# Revit family: Hager-VEGA-Surface_mounted-IP40-With_Cover-With_DIN-Hosted-ES-es
name_source: partatom
category: Electrical Equipment
units: mm (PartAtom-declared; Revit-internal decimal feet)

## family parameters
Cut with Voids When Loaded = No
Host = Face
Maintain Annotation Orientation = Yes
Panel Configuration = Two Columns, Circuits Across
Part Type = Panelboard
Room Calculation Point = No
Round Connector Dimension = Use Diameter
Shared = No

## types (13) — shared parameters
BC_MODEL_ID = 1547029
BC_OBJECT_ID = 513446
BC_OBJECT_VERSION = #3
Code hager = ADD-EC000214_EU
EF000003 - Método de montaje = Montado superficial (escayola)
EF000008 - Anchura = 400 mm  [stored 1.31234 ft]
EF000024 - Resistente a UV = No
EF000049 - Profundidad = 146 mm  [stored 0.479003 ft]
EF000116 - Número RAL = 9010
EF000118 - Con placa de montaje = No
EF001062 - Versión de CEM = No
EF001134 - Carril DIN = Yes
EF005474 - Grado de protección (IP) = IP40
EF006306 - Con candado = No
ETIM class code = EC000214
ETIM class name = Small distribution board
HG000001 - Número de columnas = 1
HG000002-with door or cover-es = Yes
HG000003-Range-es = VEGA
HG000005-Thickness-es = 2 mm  [stored 0.00656168 ft]
HG000006-Flush mounted-es = No
HG000009-Double swing door-es = No
HG000010-Asymmetric doors-es = No
HG000011-Empty rows from bottom-es = No
HG000012-Door swing angle-es = 90.00°
HG000013-Door on the left-es = No
HG000014-Door on the right-es = Yes
HG000015-Clearance visibility-es = Yes
HG000016-Door 3D visibility-es = Yes
HG000017-Distance between poles-es = 18 mm  [stored 0.0590551 ft]
HG000060-RAL-number = 9010
HG000099-Onfly Template ID-es-ES = 507532
Manufacturer = Hager
Name = VEGA-Surface_mounted-IP40-With_Cover-With_DIN-ES
Name BIM&CO = Electricity
Name hager = ADD_Enclosures_EC000214
Uniformat = Low Tension Service & Dist.
Uniformat code = D501001
zero-valued in all types: Default Elevation, EF000218 - Profundidad de instalación, EF000332 - Altura de la instalación, EF000846 - Anchura de montaje, EF001131 - Profundidad interna, HG000007-Number of empty columns-es, HG000008-Number of empty rows-es

## per-type parameters (varying)
| type | BC_VARIANT_ID | EF000007 - Color | EF000040 - Altura | EF000266 - Número de filas | EF001088 - Posibilidad de extensión | EF002950 - Ancho en número de espacios modulares | EF004462 - Tipo de cierre | EF006244 - Tapa/puerta transparente | EF009212 - Versión de la cubierta | EF015776 - Borne de tierra | EF015777 - Borne neutro | EF015941 - Puerta de transmisión de señal | HG000004-Manufacturer reference-es | HGEF000266-Número de filas | HGEF0002950-Ancho en número de espacios modulares |
| VEGA-Surface_mounted_W400_H325_D146_18_Modular_Spacing-VB118L | 1173965 | Blanco | 325 mm  [stored 1.06627 ft] | 1 | Yes | 18 | Otros | No |  | No | No | No | VB118L | 1 | 18 |
| VEGA-Surface_mounted_W400_H325_D146_18_Modular_Spacing-VB118PE | 1173966 | Blanco | 325 mm  [stored 1.06627 ft] | 1 | Yes | 18 | Otros | No | Cerrado | Yes | No | Yes | VB118PE | 1 | 18 |
| VEGA-Surface_mounted_W400_H325_D146_18_Modular_Spacing-VB118TE | 1173967 | Blanco | 325 mm  [stored 1.06627 ft] | 1 | Yes | 18 | Otros | Yes | Cerrado | Yes | No | Yes | VB118TE | 1 | 18 |
| VEGA-Surface_mounted_W400_H475_D146_36_Modular_Spacing-VB218L | 1173968 | Blanco | 475 mm  [stored 1.5584 ft] | 2 | Yes | 36 | Otros | No |  | Yes | Yes | Yes | VB218L | 2 | 36 |
| VEGA-Surface_mounted_W400_H475_D146_18_Modular_Spacing-VB218PE | 1173969 | Blanco | 475 mm  [stored 1.5584 ft] | 2 | Yes | 18 | Otros | No | Cerrado | Yes | No | Yes | VB218PE | 2 | 18 |
| VEGA-Surface_mounted_W400_H475_D146_18_Modular_Spacing-VB218R | 1173970 |  | 475 mm  [stored 1.5584 ft] | 2 | No | 18 |  | No |  | No | No | No | VB218R | 2 | 18 |
| VEGA-Surface_mounted_W400_H475_D146_18_Modular_Spacing-VB218TE | 1173971 | Blanco | 475 mm  [stored 1.5584 ft] | 2 | Yes | 18 | Otros | Yes | Cerrado | Yes | No | Yes | VB218TE | 2 | 18 |
| VEGA-Surface_mounted_W400_H625_D146_54_Modular_Spacing-VB318L | 1173972 | Blanco | 625 mm  [stored 2.05052 ft] | 3 | Yes | 54 | Otros | No |  | Yes | Yes | Yes | VB318L | 3 | 54 |
| VEGA-Surface_mounted_W400_H625_D146_18_Modular_Spacing-VB318PE | 1173973 | Blanco | 625 mm  [stored 2.05052 ft] | 3 | Yes | 18 | Otros | No | Cerrado | Yes | No | Yes | VB318PE | 3 | 18 |
| VEGA-Surface_mounted_W400_H625_D146_18_Modular_Spacing-VB318TE | 1173974 | Blanco | 625 mm  [stored 2.05052 ft] | 3 | Yes | 18 | Otros | Yes | Cerrado | Yes | No | Yes | VB318TE | 3 | 18 |
| VEGA-Surface_mounted_W400_H775_D146_72_Modular_Spacing-VB418L | 1173975 | Blanco | 775 mm  [stored 2.54265 ft] | 4 | Yes | 72 | Otros | No |  | Yes | Yes | Yes | VB418L | 4 | 72 |
| VEGA-Surface_mounted_W400_H775_D146_18_Modular_Spacing-VB418PE | 1173976 | Blanco | 775 mm  [stored 2.54265 ft] | 4 | Yes | 18 | Otros | No | Cerrado | Yes | No | Yes | VB418PE | 4 | 18 |
| VEGA-Surface_mounted_W400_H775_D146_18_Modular_Spacing-VB418TE | 1173977 | Blanco | 775 mm  [stored 2.54265 ft] | 4 | Yes | 18 | Otros | Yes | Cerrado | Yes | No | Yes | VB418TE | 4 | 18 |

note: column(s) folded — value = type name in every type: Reference

note: [stored X ft] marks values corroborated as IEEE doubles in the binary element streams (Revit-internal decimal feet)

## geometry (parser evidence)
native form markers: Sweep x14
no freeform markers — native parametric forms only
